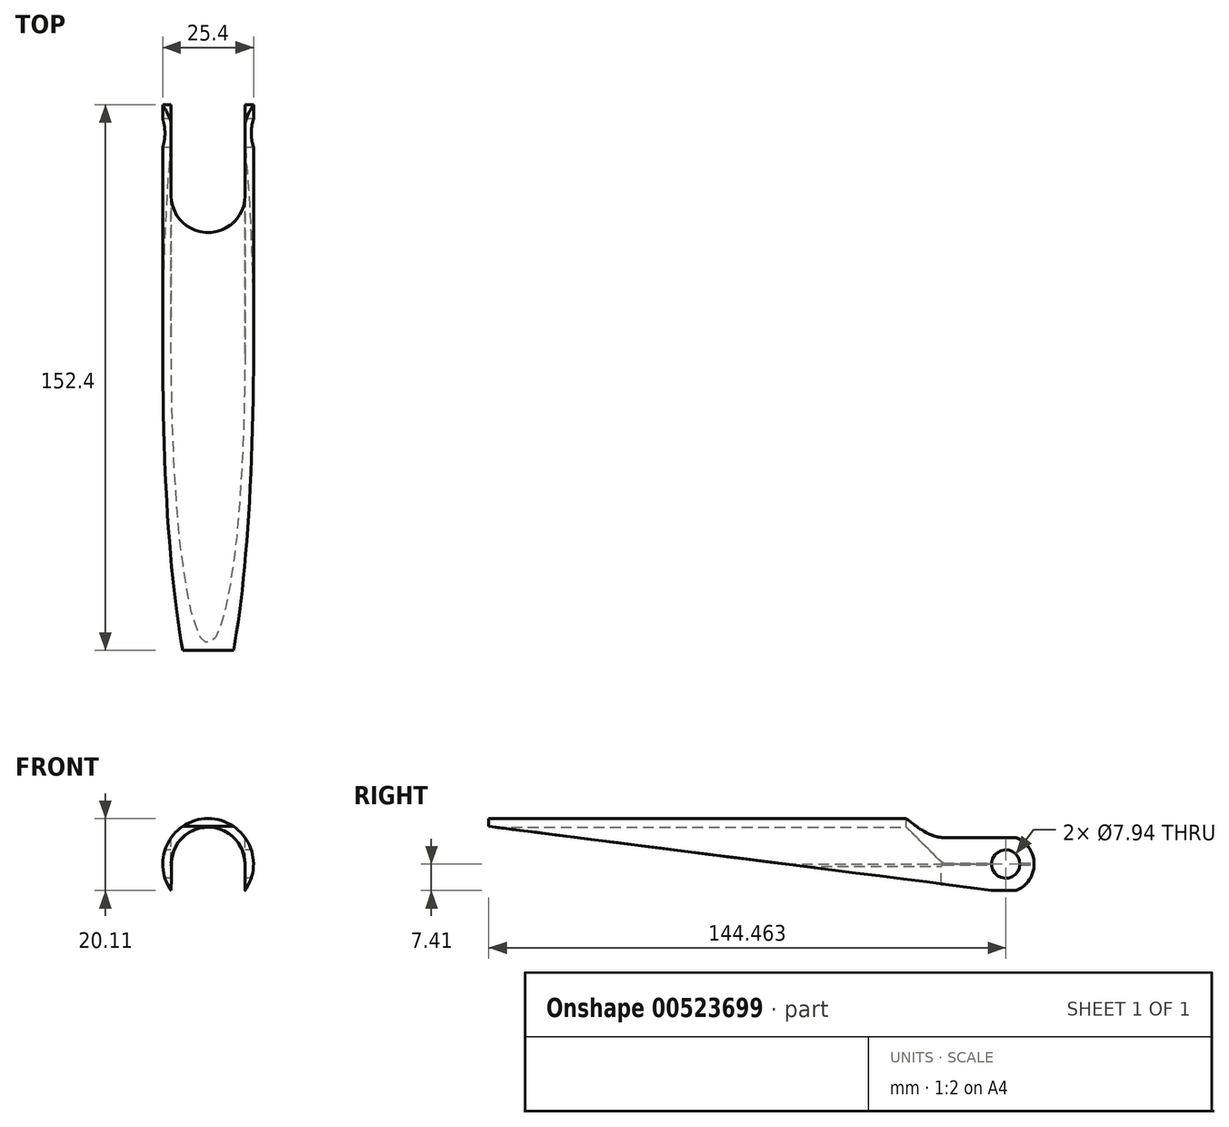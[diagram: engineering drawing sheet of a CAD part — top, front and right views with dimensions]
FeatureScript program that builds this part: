
annotation { "Feature Type Name" : "Feature", "Feature Type Description" : "" }
export const myFeature = defineFeature(function(context is Context, id is Id, definition is map)
    precondition{}
    {
        {
            var Q0;
            Q0=qCreatedBy(makeId("Front.planeOp"),FACE);
            var sketch = newSketch(context, id + "F0", { "sketchPlane" : qUnion([Q0])});
            skCircle(sketch, "E0", {"center": v(0, 0) * mm, "radius": 12.7 * mm});
            skCircle(sketch, "E1", {"center": v(0, 0) * mm, "radius": 10.32 * mm});
            skSolve(sketch);
        }
        {
            var Q0;
            Q0=makeQuery(id+"F0.imprint","IMPRINT",FACE,{"disambiguationData":[TD([[makeQuery(id+"F0.imprint","IMPRINT",EDGE,{"derivedFrom":sQuery(id+"F0.wireOp",EDGE,"E0")}),1.0]])]});
            var Q1;
            Q1=sQuery(id+"F0.wireOp",EDGE,"E0");
            extrude(context, id + "F1", {"entities" : qUnion([Q0]), "surfaceEntities" : qUnion([Q1]), "depth" : 152.4 * mm, "offsetDistance" : 25.4 * mm});
        }
        {
            var Q0;
            Q0=qCreatedBy(makeId("Right.planeOp"),FACE);
            var sketch = newSketch(context, id + "F2", { "sketchPlane" : qUnion([Q0])});
            skLineSegment(sketch, "E2", {"start": v(0, 0) * mm, "end": v(-7.94, 0) * mm, "construction": true});
            skCircle(sketch, "E3", {"center": v(-7.94, 0) * mm, "radius": 3.97 * mm});
            skSolve(sketch);
        }
        {
            var Q0;
            Q0 = qSketchRegion(id + "F2", true);
            extrude(context, id + "F3", {"entities" : qUnion([Q0]), "operationType" : NewBodyOperationType.REMOVE, "endBound" : BoundingType.SYMMETRIC, "depth" : 25.4 * mm, "offsetDistance" : 25.4 * mm, "hasSecondDirection" : true, "secondDirectionOppositeDirection" : true, "secondDirectionDepth" : 25.4 * mm});
        }
        {
            var Q0;
            Q0=qCreatedBy(makeId("Top.planeOp"),FACE);
            var sketch = newSketch(context, id + "F4", { "sketchPlane" : qUnion([Q0])});
            skLineSegment(sketch, "E4", {"start": v(-10.32, -25.4) * mm, "end": v(-10.32, 0) * mm});
            skLineSegment(sketch, "E5", {"start": v(10.32, -25.4) * mm, "end": v(10.32, 0) * mm});
            skLineSegment(sketch, "E6", {"start": v(-10.32, 0) * mm, "end": v(10.32, 0) * mm});
            skArc(sketch, "E7", {"start": v(-10.32, -25.4) * mm, "mid": v(0, -35.72) * mm, "end": v(10.32, -25.4) * mm});
            skSolve(sketch);
        }
        {
            var Q0;
            Q0 = qSketchRegion(id + "F4", true);
            extrude(context, id + "F5", {"entities" : qUnion([Q0]), "operationType" : NewBodyOperationType.REMOVE, "endBound" : BoundingType.SYMMETRIC, "oppositeDirection" : true, "depth" : 25.4 * mm, "offsetDistance" : 25.4 * mm});
        }
        {
            var Q0;
            Q0=qCreatedBy(makeId("Right.planeOp"),FACE);
            var sketch = newSketch(context, id + "F6", { "sketchPlane" : qUnion([Q0])});
            skLineSegment(sketch, "E8", {"start": v(0, -7.31) * mm, "end": v(-11.9, -7.31) * mm, "construction": true});
            skLineSegment(sketch, "E9", {"start": v(-152.4, 10.53) * mm, "end": v(-152.4, -12.87) * mm});
            skLineSegment(sketch, "E10", {"start": v(-152.4, -12.87) * mm, "end": v(-11.96, -12.87) * mm});
            skLineSegment(sketch, "E11", {"start": v(-11.96, -12.87) * mm, "end": v(-11.9, -7.31) * mm});
            skLineSegment(sketch, "E12", {"start": v(-152.4, 10.53) * mm, "end": v(-11.9, -7.31) * mm});
            skSolve(sketch);
        }
        {
            var Q0;
            Q0 = qSketchRegion(id + "F6", true);
            extrude(context, id + "F7", {"entities" : qUnion([Q0]), "operationType" : NewBodyOperationType.REMOVE, "endBound" : BoundingType.SYMMETRIC, "oppositeDirection" : true, "depth" : 25.4 * mm, "offsetDistance" : 25.4 * mm});
        }
        {
            var Q0;
            Q0=qCreatedBy(makeId("Front.planeOp"),FACE);
            var sketch = newSketch(context, id + "F8", { "sketchPlane" : qUnion([Q0])});
            skLineSegment(sketch, "E13.bottom", {"start": v(-10.3, 0) * mm, "end": v(10.34, 0) * mm});
            skLineSegment(sketch, "E13.top", {"start": v(-10.3, -12.7) * mm, "end": v(10.34, -12.7) * mm});
            skLineSegment(sketch, "E13.left", {"start": v(-10.3, 0) * mm, "end": v(-10.3, -12.7) * mm});
            skLineSegment(sketch, "E13.right", {"start": v(10.34, 0) * mm, "end": v(10.34, -12.7) * mm});
            skSolve(sketch);
        }
        {
            var Q0;
            Q0=makeQuery(id+"F8.imprint","IMPRINT",FACE,{"disambiguationData":[TD([[makeQuery(id+"F8.imprint","IMPRINT",EDGE,{"derivedFrom":sQuery(id+"F8.wireOp",EDGE,"E13.bottom")}),-1.0]])]});
            extrude(context, id + "F9", {"entities" : qUnion([Q0]), "operationType" : NewBodyOperationType.REMOVE, "depth" : 127 * mm, "offsetDistance" : 25.4 * mm});
        }
        {
            var Q0;
            Q0=qCreatedBy(makeId("Right.planeOp"),FACE);
            var sketch = newSketch(context, id + "F10", { "sketchPlane" : qUnion([Q0])});
            skArc(sketch, "E14", {"start": v(-7.94, -7.94) * mm, "mid": v(0, 0) * mm, "end": v(-7.94, 7.94) * mm});
            skLineSegment(sketch, "E15", {"start": v(0, 0) * mm, "end": v(0, 7.94) * mm});
            skLineSegment(sketch, "E16", {"start": v(0, 7.94) * mm, "end": v(-7.94, 7.94) * mm});
            skLineSegment(sketch, "E17", {"start": v(0, 0) * mm, "end": v(0, -7.94) * mm});
            skLineSegment(sketch, "E18", {"start": v(0, -7.94) * mm, "end": v(-7.94, -7.94) * mm});
            skSolve(sketch);
        }
        {
            var Q0;
            Q0 = qSketchRegion(id + "F10", true);
            extrude(context, id + "F11", {"entities" : qUnion([Q0]), "operationType" : NewBodyOperationType.REMOVE, "endBound" : BoundingType.SYMMETRIC, "oppositeDirection" : true, "depth" : 25.4 * mm, "offsetDistance" : 25.4 * mm});
        }
    });
